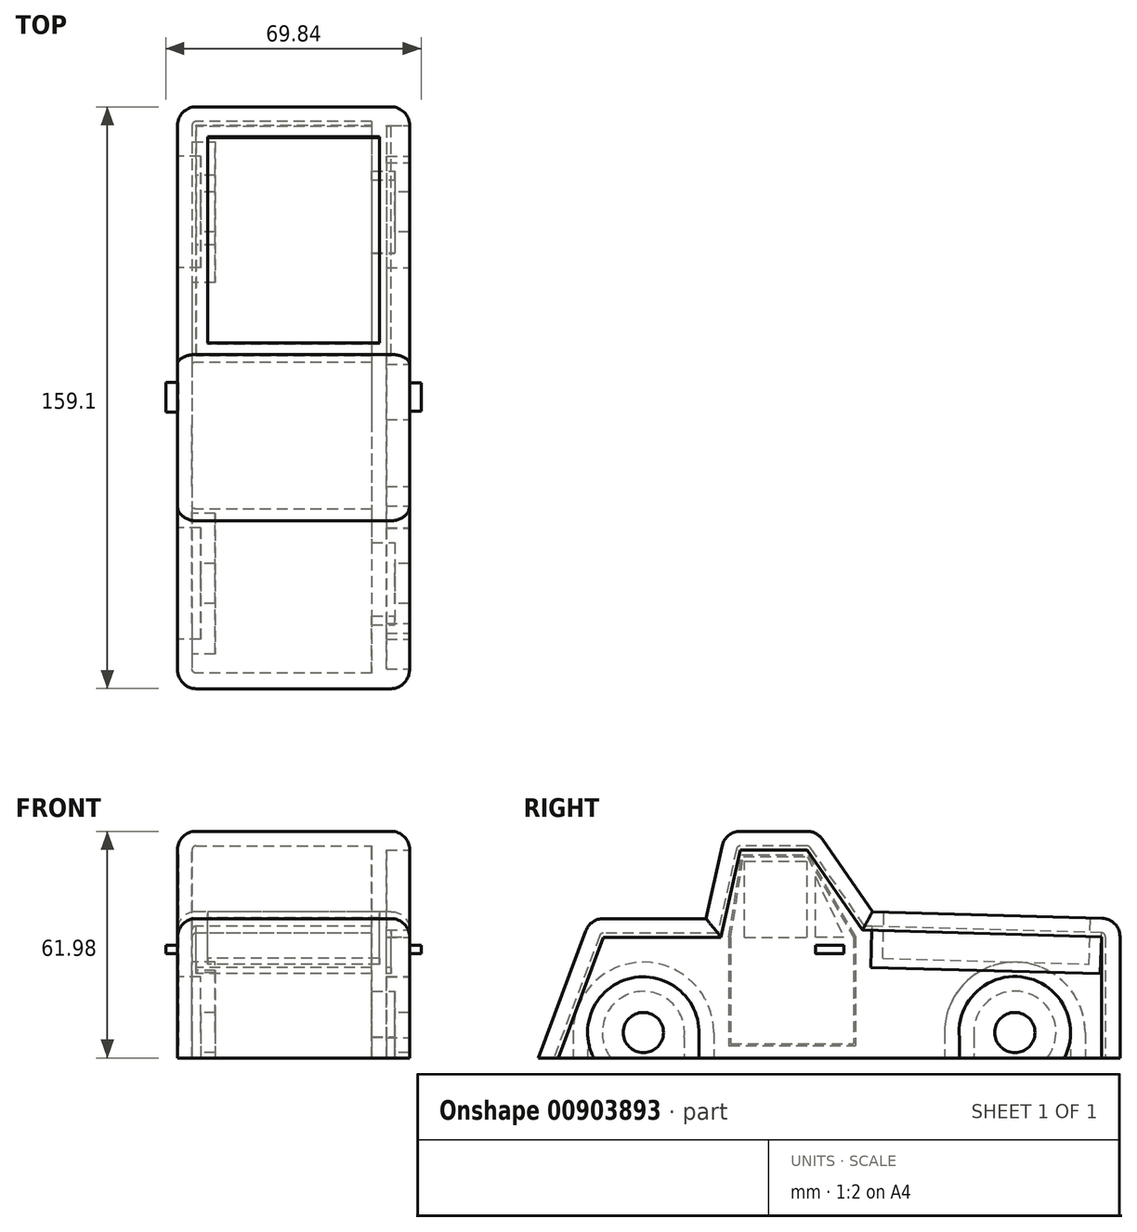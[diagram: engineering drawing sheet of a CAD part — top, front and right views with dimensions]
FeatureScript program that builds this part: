
annotation { "Feature Type Name" : "Feature", "Feature Type Description" : "" }
export const myFeature = defineFeature(function(context is Context, id is Id, definition is map)
    precondition{}
    {
        {
            var Q0;
            Q0=qCreatedBy(makeId("Right.planeOp"),FACE);
            var sketch = newSketch(context, id + "F0", { "sketchPlane" : qUnion([Q0])});
            skLineSegment(sketch, "E0.bottom", {"start": v(79.55, -19.05) * mm, "end": v(-3.35, -19.05) * mm});
            skLineSegment(sketch, "E0.left", {"start": v(79.55, -19.05) * mm, "end": v(79.55, 19.05) * mm});
            skPoint(sketch, "E0.middle", {"position": v(38.1, 0) * mm});
            skLineSegment(sketch, "E1", {"start": v(-3.35, -19.05) * mm, "end": v(-79.55, -19.05) * mm});
            skLineSegment(sketch, "E2", {"start": v(-79.55, -19.05) * mm, "end": v(-65.28, 19.05) * mm});
            skLineSegment(sketch, "E3", {"start": v(-65.28, 19.05) * mm, "end": v(-33.65, 19.05) * mm});
            skLineSegment(sketch, "E4", {"start": v(-33.65, 19.05) * mm, "end": v(-28.37, 42.93) * mm});
            skLineSegment(sketch, "E5", {"start": v(-28.37, 42.93) * mm, "end": v(-3.35, 42.93) * mm});
            skLineSegment(sketch, "E6", {"start": v(-3.35, 42.93) * mm, "end": v(11.86, 20.96) * mm});
            skLineSegment(sketch, "E7", {"start": v(11.86, 20.96) * mm, "end": v(79.55, 19.05) * mm});
            skSolve(sketch);
        }
        {
            var Q0;
            Q0 = qSketchRegion(id + "F0", true);
            extrude(context, id + "F1", {"entities" : qUnion([Q0]), "endBound" : BoundingType.SYMMETRIC, "depth" : 63.5 * mm, "offsetDistance" : 25.4 * mm});
        }
        {
            var Q0;
            Q0=makeQuery(id+"F1.opExtrude","SWEPT_EDGE",EDGE,{"disambiguationData":[OSD([sQuery(id+"F0.wireOp",EDGE,"E2"),sQuery(id+"F0.wireOp",EDGE,"E3")])]});
            var Q1;
            Q1=makeQuery(id+"F1.opExtrude","CAP_EDGE",EDGE,{"disambiguationData":[OSD([sQuery(id+"F0.wireOp",EDGE,"E2")])],"isStart":false});
            var Q2;
            Q2=makeQuery(id+"F1.opExtrude","CAP_EDGE",EDGE,{"disambiguationData":[OSD([sQuery(id+"F0.wireOp",EDGE,"E2")])],"isStart":true});
            var Q3;
            Q3=makeQuery(id+"F1.opExtrude","CAP_EDGE",EDGE,{"disambiguationData":[OSD([sQuery(id+"F0.wireOp",EDGE,"E3")])],"isStart":false});
            var Q4;
            Q4=makeQuery(id+"F1.opExtrude","CAP_EDGE",EDGE,{"disambiguationData":[OSD([sQuery(id+"F0.wireOp",EDGE,"E3")])],"isStart":true});
            var Q5;
            Q5=makeQuery(id+"F1.opExtrude","CAP_EDGE",EDGE,{"disambiguationData":[OSD([sQuery(id+"F0.wireOp",EDGE,"E4")])],"isStart":false});
            var Q6;
            Q6=makeQuery(id+"F1.opExtrude","CAP_EDGE",EDGE,{"disambiguationData":[OSD([sQuery(id+"F0.wireOp",EDGE,"E4")])],"isStart":true});
            var Q7;
            Q7=makeQuery(id+"F1.opExtrude","SWEPT_EDGE",EDGE,{"disambiguationData":[OSD([sQuery(id+"F0.wireOp",EDGE,"E4"),sQuery(id+"F0.wireOp",EDGE,"E5")])]});
            var Q8;
            Q8=makeQuery(id+"F1.opExtrude","SWEPT_FACE",FACE,{"disambiguationData":[OSD([sQuery(id+"F0.wireOp",EDGE,"E5")])]});
            var Q9;
            Q9=makeQuery(id+"F1.opExtrude","CAP_EDGE",EDGE,{"disambiguationData":[OSD([sQuery(id+"F0.wireOp",EDGE,"E6")])],"isStart":false});
            var Q10;
            Q10=makeQuery(id+"F1.opExtrude","CAP_EDGE",EDGE,{"disambiguationData":[OSD([sQuery(id+"F0.wireOp",EDGE,"E7")])],"isStart":false});
            var Q11;
            Q11=makeQuery(id+"F1.opExtrude","SWEPT_EDGE",EDGE,{"disambiguationData":[OSD([sQuery(id+"F0.wireOp",EDGE,"E0.left"),sQuery(id+"F0.wireOp",EDGE,"E7")])]});
            var Q12;
            Q12=makeQuery(id+"F1.opExtrude","CAP_EDGE",EDGE,{"disambiguationData":[OSD([sQuery(id+"F0.wireOp",EDGE,"E7")])],"isStart":true});
            var Q13;
            Q13=makeQuery(id+"F1.opExtrude","CAP_EDGE",EDGE,{"disambiguationData":[OSD([sQuery(id+"F0.wireOp",EDGE,"E6")])],"isStart":true});
            var Q14;
            Q14=makeQuery(id+"F1.opExtrude","CAP_EDGE",EDGE,{"disambiguationData":[OSD([sQuery(id+"F0.wireOp",EDGE,"E0.left")])],"isStart":true});
            var Q15;
            Q15=makeQuery(id+"F1.opExtrude","CAP_EDGE",EDGE,{"disambiguationData":[OSD([sQuery(id+"F0.wireOp",EDGE,"E0.left")])],"isStart":false});
            fillet(context, id + "F2", {"entities" : qUnion([Q0, Q1, Q2, Q3, Q4, Q5, Q6, Q7, Q8, Q9, Q10, Q11, Q12, Q13, Q14, Q15]), "radius" : 5.08 * mm, "tangentPropagation" : true, "allowEdgeOverflow" : false});
        }
        {
            var Q0;
            Q0=makeQuery(id+"F1.opExtrude","CAP_FACE",FACE,{"disambiguationData":[OSD([sQuery(id+"F0.wireOp",EDGE,"E0.bottom"),sQuery(id+"F0.wireOp",EDGE,"E0.left"),sQuery(id+"F0.wireOp",EDGE,"E1"),sQuery(id+"F0.wireOp",EDGE,"E2"),sQuery(id+"F0.wireOp",EDGE,"E3"),sQuery(id+"F0.wireOp",EDGE,"E4"),sQuery(id+"F0.wireOp",EDGE,"E5"),sQuery(id+"F0.wireOp",EDGE,"E6"),sQuery(id+"F0.wireOp",EDGE,"E7")])],"isStart":true});
            var sketch = newSketch(context, id + "F3", { "sketchPlane" : qUnion([Q0])});
            skCircle(sketch, "E8", {"center": v(-50.8, -12.1) * mm, "radius": 15.24 * mm});
            skCircle(sketch, "E9", {"center": v(50.8, -12.1) * mm, "radius": 15.24 * mm});
            skLineSegment(sketch, "E10", {"start": v(-66.04, -10.61) * mm, "end": v(-66.04, -19.05) * mm});
            skLineSegment(sketch, "E11", {"start": v(-35.56, -12.1) * mm, "end": v(-35.56, -19.05) * mm});
            skLineSegment(sketch, "E12.MirrorCS", {"start": v(35.56, -12.1) * mm, "end": v(35.56, -19.05) * mm});
            skLineSegment(sketch, "E13.MirrorCS", {"start": v(66.04, -10.61) * mm, "end": v(66.04, -19.05) * mm});
            skSolve(sketch);
        }
        {
            var Q0;
            {var subQ0=sQuery(id+"F3.wireOp",EDGE,"E8");var subQ1=makeQuery(id+"F3.imprint","INTERSECT",VERTEX,{"derivedFrom":[subQ0,sQuery(id+"F3.wireOp",EDGE,"E11")]});Q0=makeQuery(id+"F3.imprint","IMPRINT",FACE,{"disambiguationData":[TD([[makeQuery(id+"F3.imprint","IMPRINT",EDGE,{"disambiguationData":[TD([[subQ1,-1.0]])],"derivedFrom":subQ0}),1.0]])]});}
            var Q1;
            {var subQ0=sQuery(id+"F3.wireOp",EDGE,"E10");var subQ1=sQuery(id+"F3.wireOp",EDGE,"E8");var subQ2=makeQuery(id+"F3.imprint","INTERSECT",VERTEX,{"derivedFrom":[subQ1,subQ0]});Q1=makeQuery(id+"F3.imprint","IMPRINT",FACE,{"disambiguationData":[TD([[makeQuery(id+"F3.imprint","IMPRINT",EDGE,{"disambiguationData":[TD([[subQ2,-1.0]])],"derivedFrom":subQ1}),-1.0]])]});}
            var Q2;
            {var subQ0=sQuery(id+"F3.wireOp",EDGE,"E11");Q2=makeQuery(id+"F3.imprint","IMPRINT",FACE,{"disambiguationData":[TD([[makeQuery(id+"F3.imprint","IMPRINT",EDGE,{"derivedFrom":subQ0}),-1.0]])]});}
            var Q3;
            {var subQ0=sQuery(id+"F3.wireOp",EDGE,"E9");var subQ1=makeQuery(id+"F3.imprint","INTERSECT",VERTEX,{"derivedFrom":[subQ0,sQuery(id+"F3.wireOp",EDGE,"E12.MirrorCS")]});Q3=makeQuery(id+"F3.imprint","IMPRINT",FACE,{"disambiguationData":[TD([[makeQuery(id+"F3.imprint","IMPRINT",EDGE,{"disambiguationData":[TD([[subQ1,1.0]])],"derivedFrom":subQ0}),1.0]])]});}
            var Q4;
            {var subQ0=sQuery(id+"F3.wireOp",EDGE,"E12.MirrorCS");Q4=makeQuery(id+"F3.imprint","IMPRINT",FACE,{"disambiguationData":[TD([[makeQuery(id+"F3.imprint","IMPRINT",EDGE,{"derivedFrom":subQ0}),1.0]])]});}
            var Q5;
            {var subQ0=sQuery(id+"F3.wireOp",EDGE,"E13.MirrorCS");var subQ1=sQuery(id+"F3.wireOp",EDGE,"E9");var subQ2=makeQuery(id+"F3.imprint","INTERSECT",VERTEX,{"derivedFrom":[subQ1,subQ0]});Q5=makeQuery(id+"F3.imprint","IMPRINT",FACE,{"disambiguationData":[TD([[makeQuery(id+"F3.imprint","IMPRINT",EDGE,{"disambiguationData":[TD([[subQ2,1.0]])],"derivedFrom":subQ1}),-1.0]])]});}
            extrude(context, id + "F4", {"entities" : qUnion([Q0, Q1, Q2, Q3, Q4, Q5]), "operationType" : NewBodyOperationType.REMOVE, "oppositeDirection" : true, "depth" : 6.35 * mm, "offsetDistance" : 25.4 * mm});
        }
        {
            var Q0;
            Q0=makeQuery(id+"F1.opExtrude","CAP_FACE",FACE,{"disambiguationData":[OSD([sQuery(id+"F0.wireOp",EDGE,"E0.bottom"),sQuery(id+"F0.wireOp",EDGE,"E0.left"),sQuery(id+"F0.wireOp",EDGE,"E1"),sQuery(id+"F0.wireOp",EDGE,"E2"),sQuery(id+"F0.wireOp",EDGE,"E3"),sQuery(id+"F0.wireOp",EDGE,"E4"),sQuery(id+"F0.wireOp",EDGE,"E5"),sQuery(id+"F0.wireOp",EDGE,"E6"),sQuery(id+"F0.wireOp",EDGE,"E7")])],"isStart":false});
            var sketch = newSketch(context, id + "F5", { "sketchPlane" : qUnion([Q0])});
            skCircle(sketch, "E14", {"center": v(50.8, -12.03) * mm, "radius": 15.24 * mm});
            skCircle(sketch, "E15", {"center": v(-50.8, -12.1) * mm, "radius": 15.24 * mm});
            skLineSegment(sketch, "E16", {"start": v(66.04, -10.61) * mm, "end": v(66.04, -19.05) * mm});
            skLineSegment(sketch, "E17", {"start": v(35.63, -10.61) * mm, "end": v(35.63, -19.05) * mm});
            skLineSegment(sketch, "E18.MirrorCS", {"start": v(-35.63, -10.61) * mm, "end": v(-35.63, -19.05) * mm});
            skLineSegment(sketch, "E19.MirrorCS", {"start": v(-66.04, -10.61) * mm, "end": v(-66.04, -19.05) * mm});
            skSolve(sketch);
        }
        {
            var Q0;
            {var subQ1=sQuery(id+"F5.wireOp",EDGE,"E15");var subQ7=makeQuery(id+"F5.imprint","IMPRINT",VERTEX,{"derivedFrom":subQ1});Q0=makeQuery(id+"F5.imprint","IMPRINT",FACE,{"disambiguationData":[TD([[makeQuery(id+"F5.imprint","IMPRINT",EDGE,{"disambiguationData":[TD([[subQ7,1.0]])],"derivedFrom":subQ1}),1.0]])]});}
            var Q1;
            {var subQ0=sQuery(id+"F5.wireOp",EDGE,"E18.MirrorCS");var subQ1=sQuery(id+"F5.wireOp",EDGE,"E15");var subQ2=makeQuery(id+"F5.imprint","INTERSECT",VERTEX,{"disambiguationData":[OD(1.0)],"derivedFrom":[subQ1,subQ0]});Q1=makeQuery(id+"F5.imprint","IMPRINT",FACE,{"disambiguationData":[TD([[makeQuery(id+"F5.imprint","IMPRINT",EDGE,{"disambiguationData":[TD([[subQ2,1.0]])],"derivedFrom":subQ1}),-1.0]])]});}
            var Q2;
            {var subQ0=sQuery(id+"F5.wireOp",EDGE,"E19.MirrorCS");var subQ1=sQuery(id+"F5.wireOp",EDGE,"E15");var subQ2=makeQuery(id+"F5.imprint","INTERSECT",VERTEX,{"derivedFrom":[subQ1,subQ0]});Q2=makeQuery(id+"F5.imprint","IMPRINT",FACE,{"disambiguationData":[TD([[makeQuery(id+"F5.imprint","IMPRINT",EDGE,{"disambiguationData":[TD([[subQ2,-1.0]])],"derivedFrom":subQ1}),-1.0]])]});}
            var Q3;
            {var subQ0=sQuery(id+"F5.wireOp",EDGE,"E14");var subQ8=makeQuery(id+"F5.imprint","IMPRINT",VERTEX,{"derivedFrom":subQ0});Q3=makeQuery(id+"F5.imprint","IMPRINT",FACE,{"disambiguationData":[TD([[makeQuery(id+"F5.imprint","IMPRINT",EDGE,{"disambiguationData":[TD([[subQ8,-1.0]])],"derivedFrom":subQ0}),1.0]])]});}
            var Q4;
            {var subQ0=sQuery(id+"F5.wireOp",EDGE,"E16");var subQ1=sQuery(id+"F5.wireOp",EDGE,"E14");var subQ2=makeQuery(id+"F5.imprint","INTERSECT",VERTEX,{"derivedFrom":[subQ1,subQ0]});Q4=makeQuery(id+"F5.imprint","IMPRINT",FACE,{"disambiguationData":[TD([[makeQuery(id+"F5.imprint","IMPRINT",EDGE,{"disambiguationData":[TD([[subQ2,1.0]])],"derivedFrom":subQ1}),-1.0]])]});}
            var Q5;
            {var subQ0=sQuery(id+"F5.wireOp",EDGE,"E17");var subQ1=sQuery(id+"F5.wireOp",EDGE,"E14");var subQ2=makeQuery(id+"F5.imprint","INTERSECT",VERTEX,{"disambiguationData":[OD(1.0)],"derivedFrom":[subQ1,subQ0]});Q5=makeQuery(id+"F5.imprint","IMPRINT",FACE,{"disambiguationData":[TD([[makeQuery(id+"F5.imprint","IMPRINT",EDGE,{"disambiguationData":[TD([[subQ2,-1.0]])],"derivedFrom":subQ1}),-1.0]])]});}
            extrude(context, id + "F6", {"entities" : qUnion([Q0, Q1, Q2, Q3, Q4, Q5]), "operationType" : NewBodyOperationType.REMOVE, "oppositeDirection" : true, "depth" : 6.35 * mm, "offsetDistance" : 25.4 * mm});
        }
        {
            var Q0;
            Q0=makeQuery(id+"F4.boolean.opBoolean","COPY",FACE,{"derivedFrom":makeQuery(id+"F4.opExtrude","CAP_FACE",FACE,{"disambiguationData":[OSD([sQuery(id+"F0.wireOp",EDGE,"E0.bottom"),sQuery(id+"F0.wireOp",EDGE,"E1"),sQuery(id+"F3.wireOp",EDGE,"E8"),sQuery(id+"F3.wireOp",EDGE,"E10"),sQuery(id+"F3.wireOp",EDGE,"E11")])],"isStart":false})});
            var sketch = newSketch(context, id + "F7", { "sketchPlane" : qUnion([Q0])});
            skCircle(sketch, "E20", {"center": v(-50.8, -12.1) * mm, "radius": 5.5 * mm});
            skCircle(sketch, "E21.MirrorC", {"center": v(50.8, -12.1) * mm, "radius": 5.5 * mm});
            skSolve(sketch);
        }
        {
            var Q0;
            Q0=makeQuery(id+"F1.opExtrude","SWEPT_FACE",FACE,{"disambiguationData":[OSD([sQuery(id+"F0.wireOp",EDGE,"E0.bottom"),sQuery(id+"F0.wireOp",EDGE,"E1")])]});
            shell(context, id + "F8", {"entities" : qUnion([Q0]), "thickness" : 4 * mm});
        }
        {
            var Q0;
            Q0 = qSketchRegion(id + "F7", true);
            extrude(context, id + "F9", {"entities" : qUnion([Q0]), "operationType" : NewBodyOperationType.REMOVE, "oppositeDirection" : true, "depth" : 63.5 * mm, "offsetDistance" : 25.4 * mm});
        }
        {
            var Q0;
            Q0=makeQuery(id+"F1.opExtrude","SWEPT_FACE",FACE,{"disambiguationData":[OSD([sQuery(id+"F0.wireOp",EDGE,"E7")])]});
            var sketch = newSketch(context, id + "F10", { "sketchPlane" : qUnion([Q0])});
            skLineSegment(sketch, "E22.bottom", {"start": v(26.67, 11.27) * mm, "end": v(-26.67, 11.27) * mm});
            skLineSegment(sketch, "E22.top", {"start": v(26.67, 74.05) * mm, "end": v(-26.67, 74.05) * mm});
            skLineSegment(sketch, "E22.left", {"start": v(26.67, 11.27) * mm, "end": v(26.67, 74.05) * mm});
            skLineSegment(sketch, "E22.right", {"start": v(-26.67, 11.27) * mm, "end": v(-26.67, 74.05) * mm});
            skSolve(sketch);
        }
        {
            var Q0;
            Q0 = qSketchRegion(id + "F10", true);
            extrude(context, id + "F11", {"entities" : qUnion([Q0]), "operationType" : NewBodyOperationType.ADD, "oppositeDirection" : true, "depth" : 15.24 * mm, "offsetDistance" : 25.4 * mm});
        }
        {
            var Q0;
            Q0=makeQuery(id+"F1.opExtrude","SWEPT_FACE",FACE,{"disambiguationData":[OSD([sQuery(id+"F0.wireOp",EDGE,"E7")])]});
            var sketch = newSketch(context, id + "F12", { "sketchPlane" : qUnion([Q0])});
            skLineSegment(sketch, "E23.bottom", {"start": v(23.5, 14.44) * mm, "end": v(-23.5, 14.44) * mm});
            skLineSegment(sketch, "E23.top", {"start": v(23.5, 70.87) * mm, "end": v(-23.5, 70.87) * mm});
            skLineSegment(sketch, "E23.left", {"start": v(23.5, 14.44) * mm, "end": v(23.5, 70.87) * mm});
            skLineSegment(sketch, "E23.right", {"start": v(-23.5, 14.44) * mm, "end": v(-23.5, 70.87) * mm});
            skPoint(sketch, "E23.middle", {"position": v(0, 42.66) * mm});
            skSolve(sketch);
        }
        {
            var Q0;
            Q0 = qSketchRegion(id + "F12", true);
            extrude(context, id + "F13", {"entities" : qUnion([Q0]), "operationType" : NewBodyOperationType.REMOVE, "oppositeDirection" : true, "depth" : 12.7 * mm, "offsetDistance" : 25.4 * mm});
        }
        {
            var Q0;
            Q0=makeQuery(id+"F1.opExtrude","CAP_FACE",FACE,{"disambiguationData":[OSD([sQuery(id+"F0.wireOp",EDGE,"E0.bottom"),sQuery(id+"F0.wireOp",EDGE,"E0.left"),sQuery(id+"F0.wireOp",EDGE,"E1"),sQuery(id+"F0.wireOp",EDGE,"E2"),sQuery(id+"F0.wireOp",EDGE,"E3"),sQuery(id+"F0.wireOp",EDGE,"E4"),sQuery(id+"F0.wireOp",EDGE,"E5"),sQuery(id+"F0.wireOp",EDGE,"E6"),sQuery(id+"F0.wireOp",EDGE,"E7")])],"isStart":true});
            var sketch = newSketch(context, id + "F14", { "sketchPlane" : qUnion([Q0])});
            skLineSegment(sketch, "E24.bottom", {"start": v(23.09, 13.97) * mm, "end": v(6.02, 13.97) * mm});
            skLineSegment(sketch, "E24.top", {"start": v(23.09, 34.74) * mm, "end": v(6.02, 34.74) * mm});
            skLineSegment(sketch, "E24.left", {"start": v(23.09, 13.97) * mm, "end": v(23.09, 34.74) * mm});
            skLineSegment(sketch, "E24.right", {"start": v(6.02, 13.97) * mm, "end": v(6.02, 34.74) * mm});
            skLineSegment(sketch, "E25", {"start": v(3.71, 13.97) * mm, "end": v(3.71, 30.5) * mm});
            skLineSegment(sketch, "E26", {"start": v(3.71, 30.5) * mm, "end": v(-4.06, 13.97) * mm});
            skLineSegment(sketch, "E27", {"start": v(-4.06, 13.97) * mm, "end": v(3.71, 13.97) * mm});
            skLineSegment(sketch, "E28", {"start": v(-6.65, 13.97) * mm, "end": v(-6.65, -15.15) * mm});
            skLineSegment(sketch, "E29", {"start": v(26.9, 13.97) * mm, "end": v(26.9, -15.15) * mm});
            skLineSegment(sketch, "E30", {"start": v(26.9, -15.15) * mm, "end": v(-6.65, -15.15) * mm});
            skLineSegment(sketch, "E31", {"start": v(26.9, 13.97) * mm, "end": v(23.45, 35.97) * mm});
            skLineSegment(sketch, "E32", {"start": v(23.45, 35.97) * mm, "end": v(6.04, 35.97) * mm});
            skLineSegment(sketch, "E33", {"start": v(6.04, 35.97) * mm, "end": v(-6.65, 13.97) * mm});
            skLineSegment(sketch, "E34.0", {"start": v(5.75, 36.48) * mm, "end": v(-7.16, 14.1) * mm});
            skLineSegment(sketch, "E34.1", {"start": v(27.41, -15.65) * mm, "end": v(-7.16, -15.65) * mm});
            skLineSegment(sketch, "E34.2", {"start": v(27.41, 14) * mm, "end": v(27.41, -15.65) * mm});
            skLineSegment(sketch, "E34.3", {"start": v(-7.16, 14.1) * mm, "end": v(-7.16, -15.65) * mm});
            skLineSegment(sketch, "E34.4", {"start": v(27.41, 14) * mm, "end": v(23.88, 36.48) * mm});
            skLineSegment(sketch, "E34.5", {"start": v(23.88, 36.48) * mm, "end": v(5.75, 36.48) * mm});
            skSolve(sketch);
        }
        {
            var Q0;
            Q0=makeQuery(id+"F14.imprint","IMPRINT",FACE,{"disambiguationData":[TD([[makeQuery(id+"F14.imprint","IMPRINT",EDGE,{"derivedFrom":sQuery(id+"F14.wireOp",EDGE,"E28")}),-1.0]])]});
            extrude(context, id + "F15", {"entities" : qUnion([Q0]), "operationType" : NewBodyOperationType.REMOVE, "oppositeDirection" : true, "depth" : 0.32 * mm, "offsetDistance" : 25.4 * mm});
        }
        {
            var Q0;
            Q0=makeQuery(id+"F14.imprint","IMPRINT",FACE,{"disambiguationData":[TD([[makeQuery(id+"F14.imprint","IMPRINT",EDGE,{"derivedFrom":sQuery(id+"F14.wireOp",EDGE,"E24.bottom")}),-1.0]])]});
            var Q1;
            Q1=makeQuery(id+"F14.imprint","IMPRINT",FACE,{"disambiguationData":[TD([[makeQuery(id+"F14.imprint","IMPRINT",EDGE,{"derivedFrom":sQuery(id+"F14.wireOp",EDGE,"E25")}),1.0]])]});
            extrude(context, id + "F16", {"entities" : qUnion([Q0, Q1]), "operationType" : NewBodyOperationType.REMOVE, "oppositeDirection" : true, "depth" : 0.32 * mm, "offsetDistance" : 25.4 * mm});
        }
        {
            var Q0;
            Q0=makeQuery(id+"F1.opExtrude","CAP_FACE",FACE,{"disambiguationData":[OSD([sQuery(id+"F0.wireOp",EDGE,"E0.bottom"),sQuery(id+"F0.wireOp",EDGE,"E0.left"),sQuery(id+"F0.wireOp",EDGE,"E1"),sQuery(id+"F0.wireOp",EDGE,"E2"),sQuery(id+"F0.wireOp",EDGE,"E3"),sQuery(id+"F0.wireOp",EDGE,"E4"),sQuery(id+"F0.wireOp",EDGE,"E5"),sQuery(id+"F0.wireOp",EDGE,"E6"),sQuery(id+"F0.wireOp",EDGE,"E7")])],"isStart":false});
            var sketch = newSketch(context, id + "F17", { "sketchPlane" : qUnion([Q0])});
            skLineSegment(sketch, "E35", {"start": v(-26.9, 13.97) * mm, "end": v(-26.9, -15.15) * mm});
            skLineSegment(sketch, "E36", {"start": v(-26.9, -15.15) * mm, "end": v(6.65, -15.15) * mm});
            skLineSegment(sketch, "E37", {"start": v(6.65, -15.15) * mm, "end": v(6.65, 13.97) * mm});
            skLineSegment(sketch, "E38", {"start": v(6.65, 13.97) * mm, "end": v(-6.04, 35.97) * mm});
            skLineSegment(sketch, "E39", {"start": v(-6.04, 35.97) * mm, "end": v(-23.45, 35.97) * mm});
            skLineSegment(sketch, "E40", {"start": v(-23.45, 35.97) * mm, "end": v(-26.9, 13.97) * mm});
            skLineSegment(sketch, "E41", {"start": v(-23.09, 34.74) * mm, "end": v(-23.09, 13.97) * mm});
            skLineSegment(sketch, "E42", {"start": v(-23.09, 13.97) * mm, "end": v(-6.02, 13.97) * mm});
            skLineSegment(sketch, "E43", {"start": v(-6.02, 34.74) * mm, "end": v(-23.09, 34.74) * mm});
            skLineSegment(sketch, "E44", {"start": v(-6.02, 34.74) * mm, "end": v(-6.02, 13.97) * mm});
            skLineSegment(sketch, "E45", {"start": v(-3.71, 13.97) * mm, "end": v(-3.71, 30.5) * mm});
            skLineSegment(sketch, "E46", {"start": v(-3.71, 30.5) * mm, "end": v(4.06, 13.97) * mm});
            skLineSegment(sketch, "E47", {"start": v(4.06, 13.97) * mm, "end": v(-3.71, 13.97) * mm});
            skLineSegment(sketch, "E48.0", {"start": v(-23.88, 36.48) * mm, "end": v(-27.41, 14) * mm});
            skLineSegment(sketch, "E48.1", {"start": v(-27.41, -15.65) * mm, "end": v(7.16, -15.65) * mm});
            skLineSegment(sketch, "E48.2", {"start": v(7.16, -15.65) * mm, "end": v(7.16, 14.1) * mm});
            skLineSegment(sketch, "E48.3", {"start": v(-27.41, 14) * mm, "end": v(-27.41, -15.65) * mm});
            skLineSegment(sketch, "E48.4", {"start": v(7.16, 14.1) * mm, "end": v(-5.75, 36.48) * mm});
            skLineSegment(sketch, "E48.5", {"start": v(-5.75, 36.48) * mm, "end": v(-23.88, 36.48) * mm});
            skSolve(sketch);
        }
        {
            var Q0;
            Q0=makeQuery(id+"F17.imprint","IMPRINT",FACE,{"disambiguationData":[TD([[makeQuery(id+"F17.imprint","IMPRINT",EDGE,{"derivedFrom":sQuery(id+"F17.wireOp",EDGE,"E41")}),1.0]])]});
            var Q1;
            Q1=makeQuery(id+"F17.imprint","IMPRINT",FACE,{"disambiguationData":[TD([[makeQuery(id+"F17.imprint","IMPRINT",EDGE,{"derivedFrom":sQuery(id+"F17.wireOp",EDGE,"E45")}),-1.0]])]});
            var Q2;
            Q2=makeQuery(id+"F17.imprint","IMPRINT",FACE,{"disambiguationData":[TD([[makeQuery(id+"F17.imprint","IMPRINT",EDGE,{"derivedFrom":sQuery(id+"F17.wireOp",EDGE,"E35")}),-1.0]])]});
            extrude(context, id + "F18", {"entities" : qUnion([Q0, Q1, Q2]), "operationType" : NewBodyOperationType.REMOVE, "oppositeDirection" : true, "depth" : 0.32 * mm, "offsetDistance" : 25.4 * mm});
        }
        {
            var Q0;
            Q0=makeQuery(id+"F18.boolean.opBoolean","SPLIT",FACE,{"disambiguationData":[TD([makeQuery(id+"F18.opExtrude","SWEPT_FACE",FACE,{"disambiguationData":[OSD([sQuery(id+"F17.wireOp",EDGE,"E35")])]})])],"derivedFrom":makeQuery(id+"F1.opExtrude","CAP_FACE",FACE,{"disambiguationData":[OSD([sQuery(id+"F0.wireOp",EDGE,"E0.bottom"),sQuery(id+"F0.wireOp",EDGE,"E0.left"),sQuery(id+"F0.wireOp",EDGE,"E1"),sQuery(id+"F0.wireOp",EDGE,"E2"),sQuery(id+"F0.wireOp",EDGE,"E3"),sQuery(id+"F0.wireOp",EDGE,"E4"),sQuery(id+"F0.wireOp",EDGE,"E5"),sQuery(id+"F0.wireOp",EDGE,"E6"),sQuery(id+"F0.wireOp",EDGE,"E7")])],"isStart":false})});
            var sketch = newSketch(context, id + "F19", { "sketchPlane" : qUnion([Q0])});
            skLineSegment(sketch, "E49.bottom", {"start": v(-3.71, 9.46) * mm, "end": v(4.06, 9.46) * mm});
            skLineSegment(sketch, "E49.top", {"start": v(-3.71, 11.76) * mm, "end": v(4.06, 11.76) * mm});
            skLineSegment(sketch, "E49.left", {"start": v(-3.71, 9.46) * mm, "end": v(-3.71, 11.76) * mm});
            skLineSegment(sketch, "E49.right", {"start": v(4.06, 9.46) * mm, "end": v(4.06, 11.76) * mm});
            skSolve(sketch);
        }
        {
            var Q0;
            Q0 = qSketchRegion(id + "F19", true);
            extrude(context, id + "F20", {"entities" : qUnion([Q0]), "operationType" : NewBodyOperationType.ADD, "depth" : 3.17 * mm, "offsetDistance" : 25.4 * mm});
        }
        {
            var Q0;
            Q0=makeQuery(id+"F14.imprint","IMPRINT",FACE,{"disambiguationData":[TD([[makeQuery(id+"F14.imprint","IMPRINT",EDGE,{"derivedFrom":sQuery(id+"F14.wireOp",EDGE,"E24.bottom")}),1.0]])]});
            var sketch = newSketch(context, id + "F21", { "sketchPlane" : qUnion([Q0])});
            skLineSegment(sketch, "E50", {"start": v(-4.18, 11.8) * mm, "end": v(3.9, 11.8) * mm});
            skLineSegment(sketch, "E51", {"start": v(3.9, 11.8) * mm, "end": v(3.9, 9.5) * mm});
            skLineSegment(sketch, "E52", {"start": v(3.9, 9.5) * mm, "end": v(-4.18, 9.5) * mm});
            skLineSegment(sketch, "E53", {"start": v(-4.18, 9.5) * mm, "end": v(-4.18, 11.8) * mm});
            skSolve(sketch);
        }
        {
            var Q0;
            Q0 = qSketchRegion(id + "F21", true);
            extrude(context, id + "F22", {"entities" : qUnion([Q0]), "operationType" : NewBodyOperationType.ADD, "depth" : 3.17 * mm, "offsetDistance" : 25.4 * mm});
        }
    });
